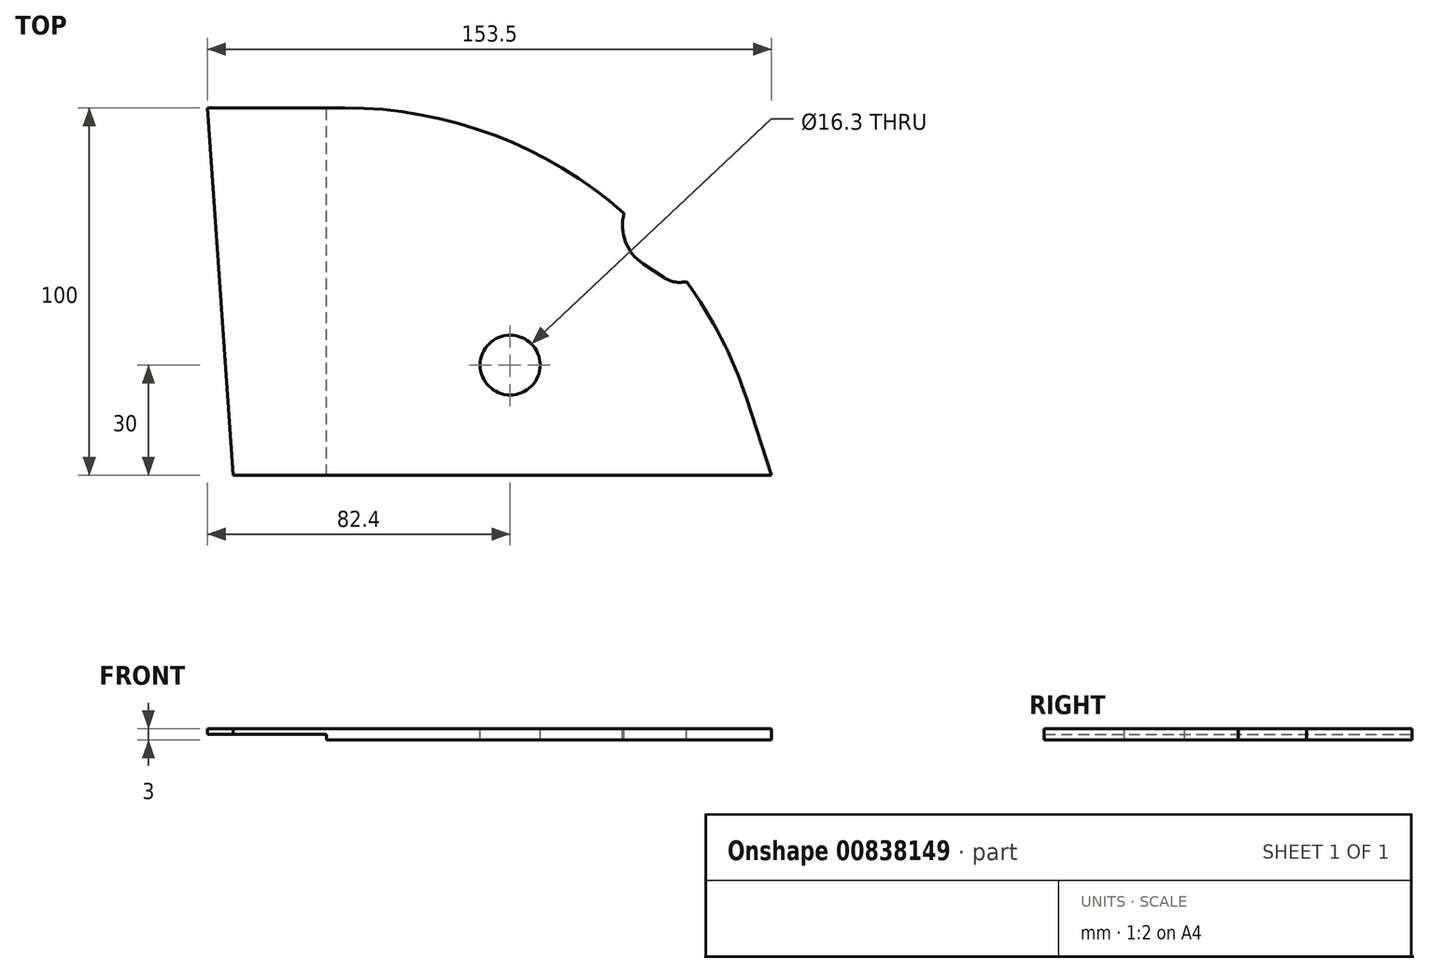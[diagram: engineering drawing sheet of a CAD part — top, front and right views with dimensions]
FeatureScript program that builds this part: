
annotation { "Feature Type Name" : "Feature", "Feature Type Description" : "" }
export const myFeature = defineFeature(function(context is Context, id is Id, definition is map)
    precondition{}
    {
        {
            var Q0;
            Q0=qCreatedBy(makeId("Top.planeOp"),FACE);
            var sketch = newSketch(context, id + "F0", { "sketchPlane" : qUnion([Q0])});
            skLineSegment(sketch, "E0", {"start": v(-202.23, 0) * mm, "end": v(-197.81, 20.8) * mm});
            skLineSegment(sketch, "E1", {"start": v(216.1, 0) * mm, "end": v(-202.23, 0) * mm});
            skLineSegment(sketch, "E2", {"start": v(-100, 100) * mm, "end": v(100, 100) * mm});
            skArc(sketch, "E3", {"start": v(-100, 100) * mm, "mid": v(-162.93, 77.71) * mm, "end": v(-197.81, 20.8) * mm});
            skArc(sketch, "E4", {"start": v(209.29, 20.8) * mm, "mid": v(167.49, 78.12) * mm, "end": v(100, 100) * mm});
            skLineSegment(sketch, "E5", {"start": v(0, 100) * mm, "end": v(0, 0) * mm, "construction": true});
            skLineSegment(sketch, "E6", {"start": v(216.1, 0) * mm, "end": v(209.29, 20.8) * mm});
            skSolve(sketch);
        }
        {
            var Q0;
            Q0=qSketchRegion(id+"F0",true);
            extrude(context, id + "F1", {"entities" : qUnion([Q0]), "depth" : 3 * mm, "offsetDistance" : 25 * mm});
        }
        {
            var Q0;
            Q0=makeQuery(id+"F1.opExtrude","CAP_FACE",FACE,{"disambiguationData":[OSD([sQuery(id+"F0.wireOp",EDGE,"E0"),sQuery(id+"F0.wireOp",EDGE,"E1"),sQuery(id+"F0.wireOp",EDGE,"E2"),sQuery(id+"F0.wireOp",EDGE,"E3"),sQuery(id+"F0.wireOp",EDGE,"E4"),sQuery(id+"F0.wireOp",EDGE,"E6")])],"isStart":false});
            var sketch = newSketch(context, id + "F2", { "sketchPlane" : qUnion([Q0])});
            skCircle(sketch, "E7", {"center": v(0, 12.5) * mm, "radius": 12.6 * mm});
            skLineSegment(sketch, "E8", {"start": v(-11.1, 18.46) * mm, "end": v(-21.76, 0) * mm});
            skLineSegment(sketch, "E9", {"start": v(11.1, 18.46) * mm, "end": v(21.76, 0) * mm});
            skLineSegment(sketch, "E10", {"start": v(21.76, 0) * mm, "end": v(-21.76, 0) * mm});
            skSolve(sketch);
        }
        {
            var Q0;
            Q0=qSketchRegion(id+"F2",true);
            extrude(context, id + "F3", {"entities" : qUnion([Q0]), "operationType" : NewBodyOperationType.REMOVE, "oppositeDirection" : true, "depth" : 25 * mm, "offsetDistance" : 25 * mm});
        }
        {
            var Q0;
            Q0=makeQuery(id+"F3.boolean.opBoolean","COPY",EDGE,{"derivedFrom":makeQuery(id+"F3.opExtrude","SWEPT_EDGE",EDGE,{"disambiguationData":[OSD([sQuery(id+"F0.wireOp",EDGE,"E1"),sQuery(id+"F2.wireOp",EDGE,"E8"),sQuery(id+"F2.wireOp",EDGE,"E10")])]})});
            var Q1;
            Q1=makeQuery(id+"F3.boolean.opBoolean","COPY",EDGE,{"derivedFrom":makeQuery(id+"F3.opExtrude","SWEPT_EDGE",EDGE,{"disambiguationData":[OSD([sQuery(id+"F0.wireOp",EDGE,"E1"),sQuery(id+"F2.wireOp",EDGE,"E9"),sQuery(id+"F2.wireOp",EDGE,"E10")])]})});
            fillet(context, id + "F4", {"entities" : qUnion([Q0, Q1]), "radius" : 5 * mm, "tangentPropagation" : true, "allowEdgeOverflow" : false});
        }
        {
            var Q0;
            Q0=makeQuery(id+"F1.opExtrude","CAP_FACE",FACE,{"disambiguationData":[OSD([sQuery(id+"F0.wireOp",EDGE,"E0"),sQuery(id+"F0.wireOp",EDGE,"E1"),sQuery(id+"F0.wireOp",EDGE,"E2"),sQuery(id+"F0.wireOp",EDGE,"E3"),sQuery(id+"F0.wireOp",EDGE,"E4"),sQuery(id+"F0.wireOp",EDGE,"E6")])],"isStart":false});
            var sketch = newSketch(context, id + "F5", { "sketchPlane" : qUnion([Q0])});
            skCircle(sketch, "E11.cCircle", {"center": v(-145, 30) * mm, "radius": 8.95 * mm, "construction": true});
            skLineSegment(sketch, "E11.0", {"start": v(-152.75, 34.47) * mm, "end": v(-145, 38.95) * mm});
            skLineSegment(sketch, "E11.1", {"start": v(-145, 38.95) * mm, "end": v(-137.25, 34.47) * mm});
            skLineSegment(sketch, "E11.2", {"start": v(-137.25, 34.47) * mm, "end": v(-137.25, 25.53) * mm});
            skLineSegment(sketch, "E11.3", {"start": v(-137.25, 25.53) * mm, "end": v(-145, 21.05) * mm});
            skLineSegment(sketch, "E11.4", {"start": v(-145, 21.05) * mm, "end": v(-152.75, 25.53) * mm});
            skLineSegment(sketch, "E11.5", {"start": v(-152.75, 25.53) * mm, "end": v(-152.75, 34.47) * mm});
            skCircle(sketch, "E12", {"center": v(-115, 30) * mm, "radius": 11.15 * mm});
            skCircle(sketch, "E13", {"center": v(-115, 60) * mm, "radius": 2.65 * mm});
            skCircle(sketch, "E14", {"center": v(-145, 60) * mm, "radius": 2.65 * mm});
            skSolve(sketch);
        }
        {
            var Q0;
            Q0=qSketchRegion(id+"F5",true);
            extrude(context, id + "F6", {"entities" : qUnion([Q0]), "operationType" : NewBodyOperationType.REMOVE, "oppositeDirection" : true, "depth" : 25 * mm, "offsetDistance" : 25 * mm});
        }
        {
            var Q0;
            Q0=makeQuery(id+"F1.opExtrude","CAP_FACE",FACE,{"disambiguationData":[OSD([sQuery(id+"F0.wireOp",EDGE,"E0"),sQuery(id+"F0.wireOp",EDGE,"E1"),sQuery(id+"F0.wireOp",EDGE,"E2"),sQuery(id+"F0.wireOp",EDGE,"E3"),sQuery(id+"F0.wireOp",EDGE,"E4"),sQuery(id+"F0.wireOp",EDGE,"E6")])],"isStart":false});
            var sketch = newSketch(context, id + "F7", { "sketchPlane" : qUnion([Q0])});
            skLineSegment(sketch, "E15.bottom", {"start": v(-39, 30) * mm, "end": v(39, 30) * mm});
            skLineSegment(sketch, "E15.top", {"start": v(-39, 85.5) * mm, "end": v(39, 85.5) * mm});
            skLineSegment(sketch, "E15.left", {"start": v(-39, 30) * mm, "end": v(-39, 85.5) * mm});
            skLineSegment(sketch, "E15.right", {"start": v(39, 30) * mm, "end": v(39, 85.5) * mm});
            skCircle(sketch, "E16", {"center": v(-42.63, 28.25) * mm, "radius": 2 * mm});
            skCircle(sketch, "E17", {"center": v(-42.63, 87.25) * mm, "radius": 2 * mm});
            skCircle(sketch, "E18", {"center": v(42.37, 87.25) * mm, "radius": 2 * mm});
            skCircle(sketch, "E19", {"center": v(42.37, 28.25) * mm, "radius": 2 * mm});
            skLineSegment(sketch, "E20", {"start": v(0, 85.5) * mm, "end": v(0, 30) * mm, "construction": true});
            skSolve(sketch);
        }
        {
            var Q0;
            Q0=qSketchRegion(id+"F7",true);
            extrude(context, id + "F8", {"entities" : qUnion([Q0]), "operationType" : NewBodyOperationType.REMOVE, "oppositeDirection" : true, "depth" : 25 * mm, "offsetDistance" : 25 * mm});
        }
        {
            var Q0;
            Q0=makeQuery(id+"F1.opExtrude","CAP_FACE",FACE,{"disambiguationData":[OSD([sQuery(id+"F0.wireOp",EDGE,"E0"),sQuery(id+"F0.wireOp",EDGE,"E1"),sQuery(id+"F0.wireOp",EDGE,"E2"),sQuery(id+"F0.wireOp",EDGE,"E3"),sQuery(id+"F0.wireOp",EDGE,"E4"),sQuery(id+"F0.wireOp",EDGE,"E6")])],"isStart":false});
            var sketch = newSketch(context, id + "F9", { "sketchPlane" : qUnion([Q0])});
            skCircle(sketch, "E21", {"center": v(145, 30) * mm, "radius": 8.15 * mm});
            skSolve(sketch);
        }
        {
            var Q0;
            Q0=qSketchRegion(id+"F9",true);
            extrude(context, id + "F10", {"entities" : qUnion([Q0]), "operationType" : NewBodyOperationType.REMOVE, "oppositeDirection" : true, "depth" : 25 * mm, "offsetDistance" : 25 * mm});
        }
        {
            var Q0;
            Q0=makeQuery(id+"F1.opExtrude","CAP_FACE",FACE,{"disambiguationData":[OSD([sQuery(id+"F0.wireOp",EDGE,"E0"),sQuery(id+"F0.wireOp",EDGE,"E1"),sQuery(id+"F0.wireOp",EDGE,"E2"),sQuery(id+"F0.wireOp",EDGE,"E3"),sQuery(id+"F0.wireOp",EDGE,"E4"),sQuery(id+"F0.wireOp",EDGE,"E6")])],"isStart":false});
            var sketch = newSketch(context, id + "F11", { "sketchPlane" : qUnion([Q0])});
            skArc(sketch, "E22", {"start": v(-100, 95) * mm, "mid": v(-155.57, 77.06) * mm, "end": v(-190.14, 30) * mm});
            skPoint(sketch, "E22.endSnap0", {"position": v(-152.75, 30) * mm});
            skLineSegment(sketch, "E23", {"start": v(-100, 95) * mm, "end": v(100, 95) * mm});
            skArc(sketch, "E24", {"start": v(200.37, 30) * mm, "mid": v(159.8, 77.33) * mm, "end": v(100, 95) * mm});
            skSolve(sketch);
        }
        {
            var Q0;
            {var subQ5=sQuery(id+"F0.wireOp",EDGE,"E0");Q0=makeQuery(id+"F11.imprint","IMPRINT",FACE,{"disambiguationData":[TD([[makeQuery(id+"F11.imprint","IMPRINT",EDGE,{"derivedFrom":makeQuery(id+"F1.opExtrude","CAP_EDGE",EDGE,{"disambiguationData":[OSD([subQ5])],"isStart":false})}),-1.0]])]});}
            var sketch = newSketch(context, id + "F12", { "sketchPlane" : qUnion([Q0])});
            skLineSegment(sketch, "E25.bottom", {"start": v(75, 0) * mm, "end": v(-232.75, 0) * mm});
            skLineSegment(sketch, "E25.top", {"start": v(75, 117.26) * mm, "end": v(-232.75, 117.26) * mm});
            skLineSegment(sketch, "E25.left", {"start": v(75, 0) * mm, "end": v(75, 117.26) * mm});
            skLineSegment(sketch, "E25.right", {"start": v(-232.75, 0) * mm, "end": v(-232.75, 117.26) * mm});
            skSolve(sketch);
        }
        {
            var Q0;
            Q0 = qSketchRegion(id + "F12", true);
            extrude(context, id + "F13", {"entities" : qUnion([Q0]), "operationType" : NewBodyOperationType.REMOVE, "oppositeDirection" : true, "depth" : 25 * mm, "offsetDistance" : 25 * mm});
        }
        {
            var Q0;
            Q0=makeQuery(id+"F1.opExtrude","CAP_FACE",FACE,{"disambiguationData":[OSD([sQuery(id+"F0.wireOp",EDGE,"E0"),sQuery(id+"F0.wireOp",EDGE,"E1"),sQuery(id+"F0.wireOp",EDGE,"E2"),sQuery(id+"F0.wireOp",EDGE,"E3"),sQuery(id+"F0.wireOp",EDGE,"E4"),sQuery(id+"F0.wireOp",EDGE,"E6")])],"isStart":true});
            var sketch = newSketch(context, id + "F14", { "sketchPlane" : qUnion([Q0])});
            skLineSegment(sketch, "E26.bottom", {"start": v(75, 0) * mm, "end": v(95, 0) * mm});
            skLineSegment(sketch, "E26.top", {"start": v(75, -100) * mm, "end": v(95, -100) * mm});
            skLineSegment(sketch, "E26.left", {"start": v(75, 0) * mm, "end": v(75, -100) * mm});
            skLineSegment(sketch, "E26.right", {"start": v(95, 0) * mm, "end": v(95, -100) * mm});
            skSolve(sketch);
        }
        {
            var Q0;
            Q0 = qSketchRegion(id + "F14", true);
            extrude(context, id + "F15", {"entities" : qUnion([Q0]), "operationType" : NewBodyOperationType.REMOVE, "oppositeDirection" : true, "depth" : 1.5 * mm, "offsetDistance" : 25 * mm});
        }
        {
            var Q0;
            {var subQ5=sQuery(id+"F0.wireOp",EDGE,"E0");Q0=makeQuery(id+"F11.imprint","IMPRINT",FACE,{"disambiguationData":[TD([[makeQuery(id+"F11.imprint","IMPRINT",EDGE,{"derivedFrom":makeQuery(id+"F1.opExtrude","CAP_EDGE",EDGE,{"disambiguationData":[OSD([subQ5])],"isStart":false})}),-1.0]])]});}
            var sketch = newSketch(context, id + "F16", { "sketchPlane" : qUnion([Q0])});
            skPoint(sketch, "E27.0", {"position": v(75, 100) * mm});
            skPoint(sketch, "E28.0", {"position": v(75, 0) * mm});
            skLineSegment(sketch, "E29", {"start": v(75, 100) * mm, "end": v(62.6, 100) * mm});
            skLineSegment(sketch, "E30", {"start": v(62.6, 100) * mm, "end": v(69.6, 0) * mm});
            skLineSegment(sketch, "E31", {"start": v(69.6, 0) * mm, "end": v(75, 0) * mm});
            skLineSegment(sketch, "E32", {"start": v(75, 100) * mm, "end": v(75, 0) * mm});
            skSolve(sketch);
        }
        {
            var Q0;
            Q0 = qSketchRegion(id + "F16", true);
            extrude(context, id + "F17", {"entities" : qUnion([Q0]), "operationType" : NewBodyOperationType.ADD, "oppositeDirection" : true, "depth" : 1.5 * mm, "offsetDistance" : 25 * mm});
        }
        {
            var Q0;
            {var subQ5=sQuery(id+"F0.wireOp",EDGE,"E0");Q0=makeQuery(id+"F11.imprint","IMPRINT",FACE,{"disambiguationData":[TD([[makeQuery(id+"F11.imprint","IMPRINT",EDGE,{"derivedFrom":makeQuery(id+"F1.opExtrude","CAP_EDGE",EDGE,{"disambiguationData":[OSD([subQ5])],"isStart":false})}),-1.0]])]});}
            var sketch = newSketch(context, id + "F18", { "sketchPlane" : qUnion([Q0])});
            skCircle(sketch, "E33", {"center": v(188.05, 68) * mm, "radius": 12.5 * mm});
            skCircle(sketch, "E34", {"center": v(191.1, 60) * mm, "radius": 7.5 * mm});
            skLineSegment(sketch, "E35", {"start": v(181.17, 57.56) * mm, "end": v(186.97, 53.74) * mm});
            skSolve(sketch);
        }
        {
            var Q0;
            Q0 = qSketchRegion(id + "F18", true);
            extrude(context, id + "F19", {"entities" : qUnion([Q0]), "operationType" : NewBodyOperationType.REMOVE, "oppositeDirection" : true, "depth" : 25 * mm, "offsetDistance" : 25 * mm});
        }
    });
